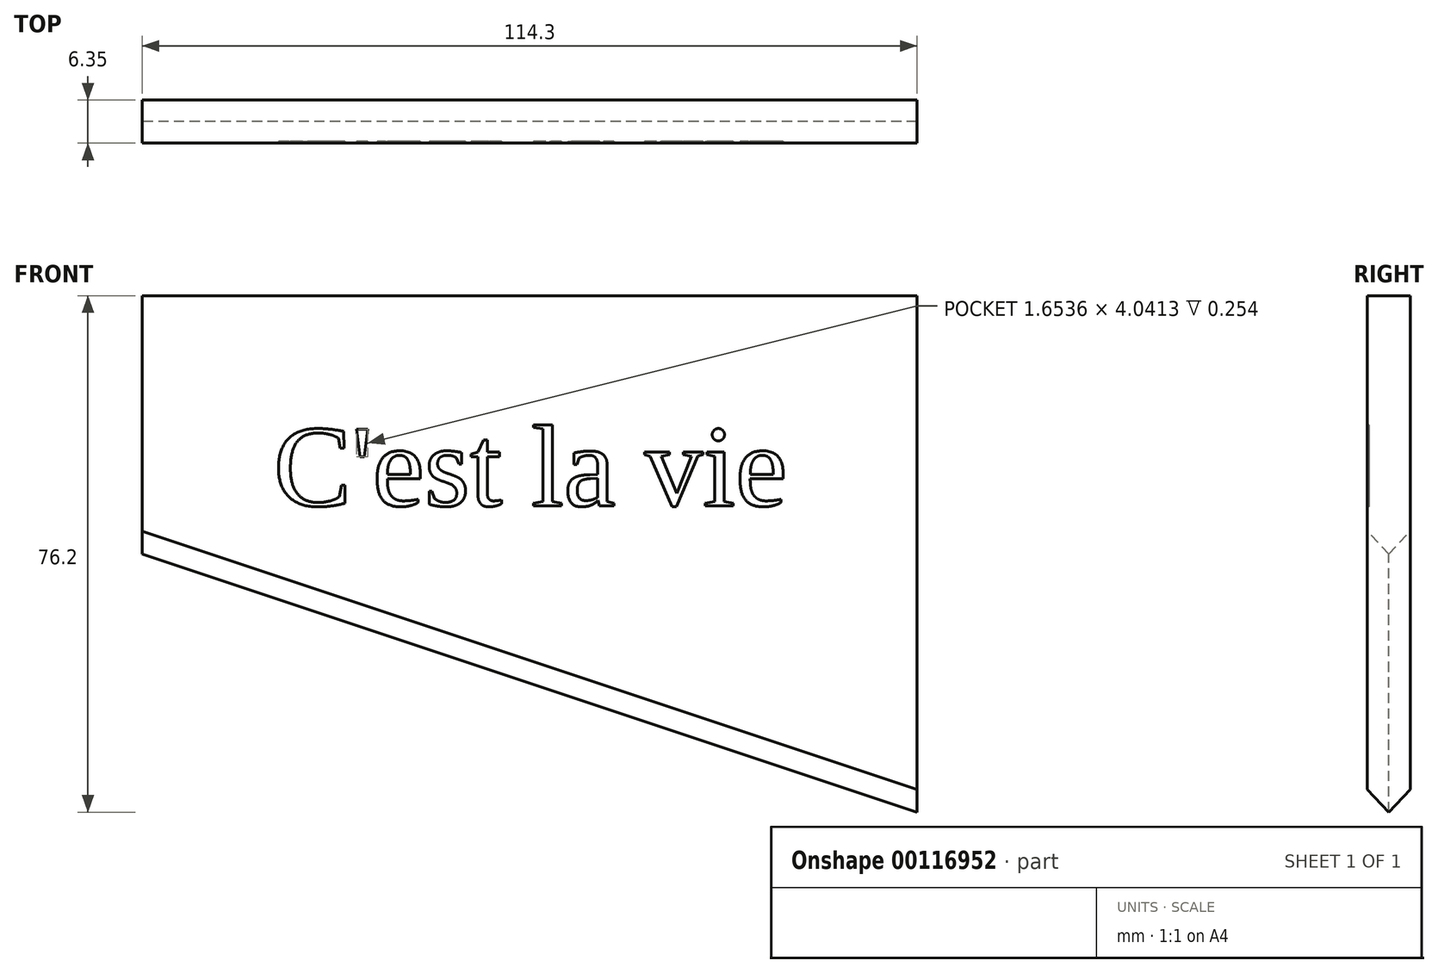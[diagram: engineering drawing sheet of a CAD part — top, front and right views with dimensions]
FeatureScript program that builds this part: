
annotation { "Feature Type Name" : "Feature", "Feature Type Description" : "" }
export const myFeature = defineFeature(function(context is Context, id is Id, definition is map)
    precondition{}
    {
        {
            var Q0;
            Q0=qCreatedBy(makeId("Front.planeOp"),FACE);
            var sketch = newSketch(context, id + "F0", { "sketchPlane" : qUnion([Q0])});
            skLineSegment(sketch, "E0.bottom", {"start": v(57.15, 38.1) * mm, "end": v(-57.15, 38.1) * mm, "construction": true});
            skLineSegment(sketch, "E0.top", {"start": v(57.15, -38.1) * mm, "end": v(-57.15, -38.1) * mm, "construction": true});
            skLineSegment(sketch, "E0.left", {"start": v(57.15, 38.1) * mm, "end": v(57.15, -38.1) * mm, "construction": true});
            skLineSegment(sketch, "E0.right", {"start": v(-57.15, 38.1) * mm, "end": v(-57.15, -38.1) * mm, "construction": true});
            skPoint(sketch, "E0.middle", {"position": v(0, 0) * mm});
            skLineSegment(sketch, "E1", {"start": v(-57.15, 38.1) * mm, "end": v(-57.15, 0) * mm});
            skLineSegment(sketch, "E2", {"start": v(-57.15, 38.1) * mm, "end": v(57.15, 38.1) * mm});
            skLineSegment(sketch, "E3", {"start": v(57.15, 38.1) * mm, "end": v(57.15, -38.1) * mm});
            skLineSegment(sketch, "E4", {"start": v(-57.15, 0) * mm, "end": v(57.15, -38.1) * mm});
            skLineSegment(sketch, "E5", {"start": v(-57.15, 0) * mm, "end": v(57.15, 0) * mm, "construction": true});
            skSolve(sketch);
        }
        {
            var Q0;
            Q0=makeQuery(id+"F0.imprint","IMPRINT",FACE,{"disambiguationData":[TD([[makeQuery(id+"F0.imprint","IMPRINT",EDGE,{"derivedFrom":sQuery(id+"F0.wireOp",EDGE,"E1")}),1.0]])]});
            extrude(context, id + "F1", {"entities" : qUnion([Q0]), "depth" : 6.35 * mm});
        }
        {
            var Q0;
            Q0=makeQuery(id+"F1.opExtrude","CAP_EDGE",EDGE,{"disambiguationData":[OSD([sQuery(id+"F0.wireOp",EDGE,"E4")])],"isStart":false});
            var Q1;
            Q1=makeQuery(id+"F1.opExtrude","CAP_EDGE",EDGE,{"disambiguationData":[OSD([sQuery(id+"F0.wireOp",EDGE,"E4")])],"isStart":true});
            chamfer(context, id + "F2", {"entities" : qUnion([Q0, Q1]), "width" : 3.17 * mm, "tangentPropagation" : true});
        }
        {
            var Q0;
            Q0=makeQuery(id+"F1.opExtrude","CAP_FACE",FACE,{"disambiguationData":[OSD([sQuery(id+"F0.wireOp",EDGE,"E1"),sQuery(id+"F0.wireOp",EDGE,"E2"),sQuery(id+"F0.wireOp",EDGE,"E3"),sQuery(id+"F0.wireOp",EDGE,"E4")])],"isStart":false});
            var sketch = newSketch(context, id + "F3", { "sketchPlane" : qUnion([Q0])});
            skText(sketch, "E6", { "text": "C\'est la vie", "fontName": "Tinos-Regular.ttf"});
            const initialGuessF3  = {"E6": [-0.03774, 0.00711, 1, 0, 0.01239]};
            skSetInitialGuess(sketch, initialGuessF3);
            skSolve(sketch);
        }
        {
            var Q0;
            Q0=qSketchRegion(id+"F3",true);
            extrude(context, id + "F4", {"entities" : qUnion([Q0]), "operationType" : NewBodyOperationType.REMOVE, "oppositeDirection" : true, "depth" : 0.25 * mm});
        }
        {
            var Q0;
            Q0=makeQuery(id+"F1.opExtrude","SWEPT_FACE",FACE,{"disambiguationData":[OSD([sQuery(id+"F0.wireOp",EDGE,"E2")])]});
            var sketch = newSketch(context, id + "F5", { "sketchPlane" : qUnion([Q0])});
            skLineSegment(sketch, "E7", {"start": v(-57.15, -3.18) * mm, "end": v(57.15, -3.18) * mm, "construction": true});
            skLineSegment(sketch, "E8", {"start": v(0, 0) * mm, "end": v(0, -6.35) * mm, "construction": true});
            skPoint(sketch, "E9", {"position": v(0, -3.18) * mm});
            skSolve(sketch);
        }
    });
